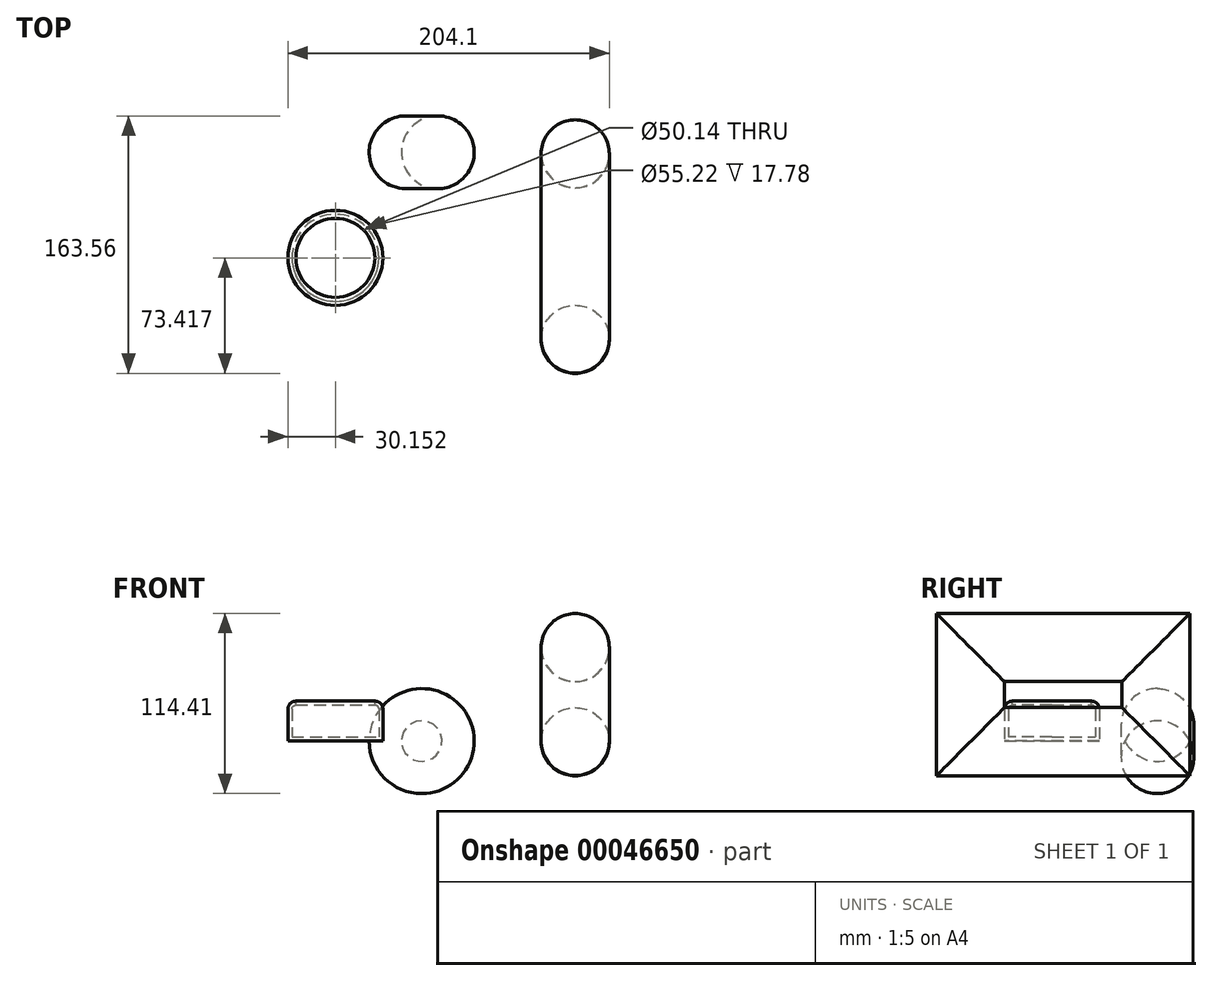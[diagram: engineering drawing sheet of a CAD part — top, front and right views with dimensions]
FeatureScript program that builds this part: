
annotation { "Feature Type Name" : "Feature", "Feature Type Description" : "" }
export const myFeature = defineFeature(function(context is Context, id is Id, definition is map)
    precondition{}
    {
        {
            var Q0;
            Q0=qCreatedBy(makeId("Top.planeOp"),FACE);
            var sketch = newSketch(context, id + "F0", { "sketchPlane" : qUnion([Q0])});
            skArc(sketch, "E0", {"start": v(0, 0) * mm, "mid": v(33.35, 20.7) * mm, "end": v(0, 41.4) * mm});
            skLineSegment(sketch, "E1", {"start": v(0, 0) * mm, "end": v(0, 41.4) * mm});
            skSolve(sketch);
        }
        {
            var Q0;
            Q0=makeQuery(id+"F0.imprint","IMPRINT",FACE,{"disambiguationData":[TD([[makeQuery(id+"F0.imprint","IMPRINT",EDGE,{"derivedFrom":sQuery(id+"F0.wireOp",EDGE,"E0")}),1.0]])]});
            var Q1;
            Q1=sQuery(id+"F0.wireOp",EDGE,"E1");
            revolve(context, id + "F1", {"entities" : qUnion([Q0]), "axis" : qUnion([Q1]), "revolveType" : RevolveType.FULL});
        }
        {
            var Q0;
            Q0=qCreatedBy(makeId("Top.planeOp"),FACE);
            var sketch = newSketch(context, id + "F2", { "sketchPlane" : qUnion([Q0])});
            skCircle(sketch, "E2", {"center": v(-54.79, -46.35) * mm, "radius": 30.15 * mm});
            skSolve(sketch);
        }
        {
            var Q0;
            Q0=makeQuery(id+"F2.imprint","IMPRINT",FACE,{"disambiguationData":[TD([[makeQuery(id+"F2.imprint","IMPRINT",EDGE,{"derivedFrom":sQuery(id+"F2.wireOp",EDGE,"E2")}),1.0]])]});
            extrude(context, id + "F3", {"entities" : qUnion([Q0]), "depth" : 25.4 * mm});
        }
        {
            var Q0;
            Q0=makeQuery(id+"F3.opExtrude","CAP_EDGE",EDGE,{"disambiguationData":[OSD([sQuery(id+"F2.wireOp",EDGE,"E2")])],"isStart":false});
            fillet(context, id + "F4", {"entities" : qUnion([Q0]), "radius" : 5.08 * mm, "tangentPropagation" : true, "allowEdgeOverflow" : false});
        }
        {
            var Q0;
            Q0=makeQuery(id+"F3.opExtrude","CAP_FACE",FACE,{"disambiguationData":[OSD([sQuery(id+"F2.wireOp",EDGE,"E2")])],"isStart":false});
            shell(context, id + "F5", {"entities" : qUnion([Q0]), "thickness" : 2.54 * mm});
        }
        {
            var Q0;
            Q0=qCreatedBy(makeId("Top.planeOp"),FACE);
            var sketch = newSketch(context, id + "F6", { "sketchPlane" : qUnion([Q0])});
            skCircle(sketch, "E3", {"center": v(97.51, 19.72) * mm, "radius": 21.65 * mm});
            skSolve(sketch);
        }
        {
            var Q0;
            Q0=qCreatedBy(makeId("Right.planeOp"),FACE);
            var Q1;
            Q1=sQuery(id+"F6.wireOp",VERTEX,"E3.center");
            cPlane(context, id + "F7", {"entities" : qUnion([Q0, Q1]), "cplaneType" : CPlaneType.PLANE_POINT, "offset" : 152.4 * mm, "width" : 152.4 * mm, "height" : 152.4 * mm});
        }
        {
            var Q0;
            Q0=qCreatedBy(id+"F7.planeOp",FACE);
            var sketch = newSketch(context, id + "F8", { "sketchPlane" : qUnion([Q0])});
            skLineSegment(sketch, "E4.bottom", {"start": v(19.33, 0) * mm, "end": v(-97.73, 0) * mm});
            skLineSegment(sketch, "E4.top", {"start": v(19.33, 59.01) * mm, "end": v(-97.73, 59.01) * mm});
            skLineSegment(sketch, "E4.left", {"start": v(19.33, 0) * mm, "end": v(19.33, 59.01) * mm});
            skLineSegment(sketch, "E4.right", {"start": v(-97.73, 0) * mm, "end": v(-97.73, 59.01) * mm});
            skSolve(sketch);
        }
        {
            var Q0;
            Q0=makeQuery(id+"F6.imprint","IMPRINT",FACE,{"disambiguationData":[TD([[makeQuery(id+"F6.imprint","IMPRINT",EDGE,{"derivedFrom":sQuery(id+"F6.wireOp",EDGE,"E3")}),1.0]])]});
            var Q1;
            Q1=sQuery(id+"F8.wireOp",EDGE,"E4.left");
            var Q2;
            Q2=sQuery(id+"F8.wireOp",EDGE,"E4.top");
            var Q3;
            Q3=sQuery(id+"F8.wireOp",EDGE,"E4.right");
            var Q4;
            Q4=sQuery(id+"F8.wireOp",EDGE,"E4.bottom");
            sweep(context, id + "F9", {"profiles" : qUnion([Q0]), "path" : qUnion([Q1, Q2, Q3, Q4])});
        }
    });
